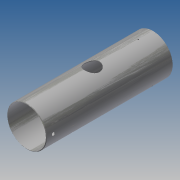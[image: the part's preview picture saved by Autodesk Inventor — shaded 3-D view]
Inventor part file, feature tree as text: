
AUTODESK INVENTOR PART (.ipt)
format: ipt  version: 2017.3 (Build 213257000, 257)  size: 205,312 bytes
history: native  units: in
note: dims shown in document units (in); Inventor stores cm internally (conversion verified against a paired STEP export)
features: extrude x7, split x5, other x5, sketch x4, plane x3, hole x3, pattern_circular x2, chamfer x2
ambient origin geometry x8: Origin, YZ Plane, XZ Plane, XY Plane, X Axis, Y Axis, Z Axis, Center Point
bodies: Solid1 (feature_tree)
feature tree (31):
  extrude  "Extrusion1"  Depth=33.0in
  plane  "Work Plane1"
  plane  "Work Plane2"
  sketch  "Sketch4"  dims[d2=108.7721in d3=0.0in d14=9.2291in]
  extrude  "Extrusion3"  Depth=108.7721in
  hole  "Hole1"  [1 undecoded]
  pattern_circular  "Circular Pattern1"  [2 undecoded]
  split  "Split1"
  split  "Split2"
  split  "Split3"
  split  "Split4"
  chamfer  "Chamfer1"  Distance=81.5359in
  hole  "Hole2"  [1 undecoded]
  pattern_circular  "Circular Pattern2"  [2 undecoded]
  plane  "Work Plane3"
  sketch  "Sketch6"  dims[d17=14.0in d18=46.9685in d19=81.5359in d20=0.0in d21=1.0in d22=0.0in d23=1.0in d24=0.0in d25=3.6875in d26=0.75in d27=0.375in d28=0.25in d29=0.5635in d30=1.0in d31=0.8108in d32=0.7874in d33=360.0deg d35=0.4375in d36=0.125in d37=0.2577in d38=12.8659in d39=0.891in d40=0.553in d41=0.0246in d42=0.897in d43=0.375in d44=0.25in d45=0.5635in d46=0.91in d47=0.8108in d48=1.1811in d49=135.0deg d51=4.125in d52=5.9063in d53=2.5625in d54=0.534in d55=0.375in d56=0.25in d57=0.5635in d58=0.891in d59=0.8108in d60=1.0in d61=0.0in d62=0.4375in d63=0.125in d64=0.2577in]
  hole  "Hole3"  [1 undecoded]
  split  "Split5"
  chamfer  "Chamfer2"  Distance=0.4375in
  sketch  "Sketch1"  dims[d0=34.0in d1=33.0in]
  other  "Srf1"
  other  "Srf2"
  other  "Srf3"
  other  "Srf4"
  sketch  "Sketch5"  dims[d15=5.25in d16=13.0in]
  other  "Srf5"
  extrude  "ExtrusionSrf1"  Depth=0.125in
  extrude  "ExtrusionSrf2"  Depth=12.8659in
  extrude  "ExtrusionSrf5"  Depth=1.1811in TaperAngle=135.0deg
  extrude  "ExtrusionSrf3"  Depth=4.125in
  extrude  "ExtrusionSrf4"  Depth=5.9063in
note: 7 required parameter values undecoded (feature->parameter linkage not recoverable at this tier; creation-order binding heuristic only, values carry confidence <= 0.55)
